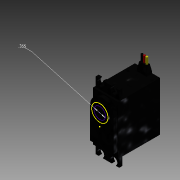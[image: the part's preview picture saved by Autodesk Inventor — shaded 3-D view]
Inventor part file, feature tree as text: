
AUTODESK INVENTOR PART (.ipt)
format: ipt  version: 2013 (Build 170138000, 138)  size: 206,848 bytes
history: native  units: in
note: dims shown in document units (in); Inventor stores cm internally (conversion verified against a paired STEP export)
features: sketch x10, extrude x9, other x4, fillet x2, plane x1, mirror x1, projected_geometry x1, hole x1
ambient origin geometry x8: Origin, YZ Plane, XZ Plane, XY Plane, X Axis, Y Axis, Z Axis, Center Point
feature tree (29):
  other  "Servo"
  other  "Blocks"
  extrude  "Extrusion1"  Depth=1.525in
  extrude  "Extrusion2"  Depth=0.025in
  extrude  "Extrusion3"  Depth=0.17in
  fillet  "Fillet1"  Radius=0.11in
  plane  "Work Plane1"
  extrude  "Extrusion4"  Depth=0.391in
  fillet  "Fillet2"  Radius=0.07in
  mirror  "Mirror1"
  extrude  "Extrusion5"  [1 undecoded]
  extrude  "Extrusion6"  Depth=0.28in
  extrude  "Extrusion7"  Depth=0.165in
  extrude  "Extrusion8"  Depth=0.1in TaperAngle=0.0deg
  extrude  "Extrusion9"  Depth=0.3in
  sketch  "Sketch25"  dims[d27=0.17in d28=0.01in d29=0.0625in d30=0.0in d31=0.2in d32=-0.0687in d33=0.0625in d34=0.2in d35=0.0in d36=0.0625in d37=0.04in d38=0.2in d39=0.0in d40=0.0625in d41=0.04in d42=0.2in d43=0.0in d140=0.6299in d141=0.1457in d142=0.6299in d143=0.6299in d144=0.315in d145=0.355in]
  sketch  "Sketch1"  dims[d0=0.782in d1=1.525in]
  sketch  "Sketch2"  dims[d2=1.305in d3=0.0in d4=0.025in]
  sketch  "Sketch3"  dims[d5=0.025in d6=0.17in d7=0.11in d8=0.0in]
  sketch  "Sketch4"  dims[d9=0.508in d11=0.391in d12=0.07in d13=0.0in]
  sketch  "Sketch5"  dims[d14=0.366in d15=-0.16in]
  sketch  "Sketch6"  dims[d16=0.737in d18=0.28in]
  sketch  "Sketch7"  dims[d19=0.1in d20=0.21in d21=0.165in]
  other  "Red wire"
  sketch  "Sketch8"  dims[d22=0.165in d23=0.1in d24=0.0in]
  sketch  "Sketch9"  dims[d25=0.01in d26=0.3in]
  other  "Yellow Wire"
  projected_geometry  "Project Cut Edges1"
  hole  "Hole Pattern 4"  [1 undecoded]
note: 2 required parameter values undecoded (feature->parameter linkage not recoverable at this tier; creation-order binding heuristic only, values carry confidence <= 0.55)
